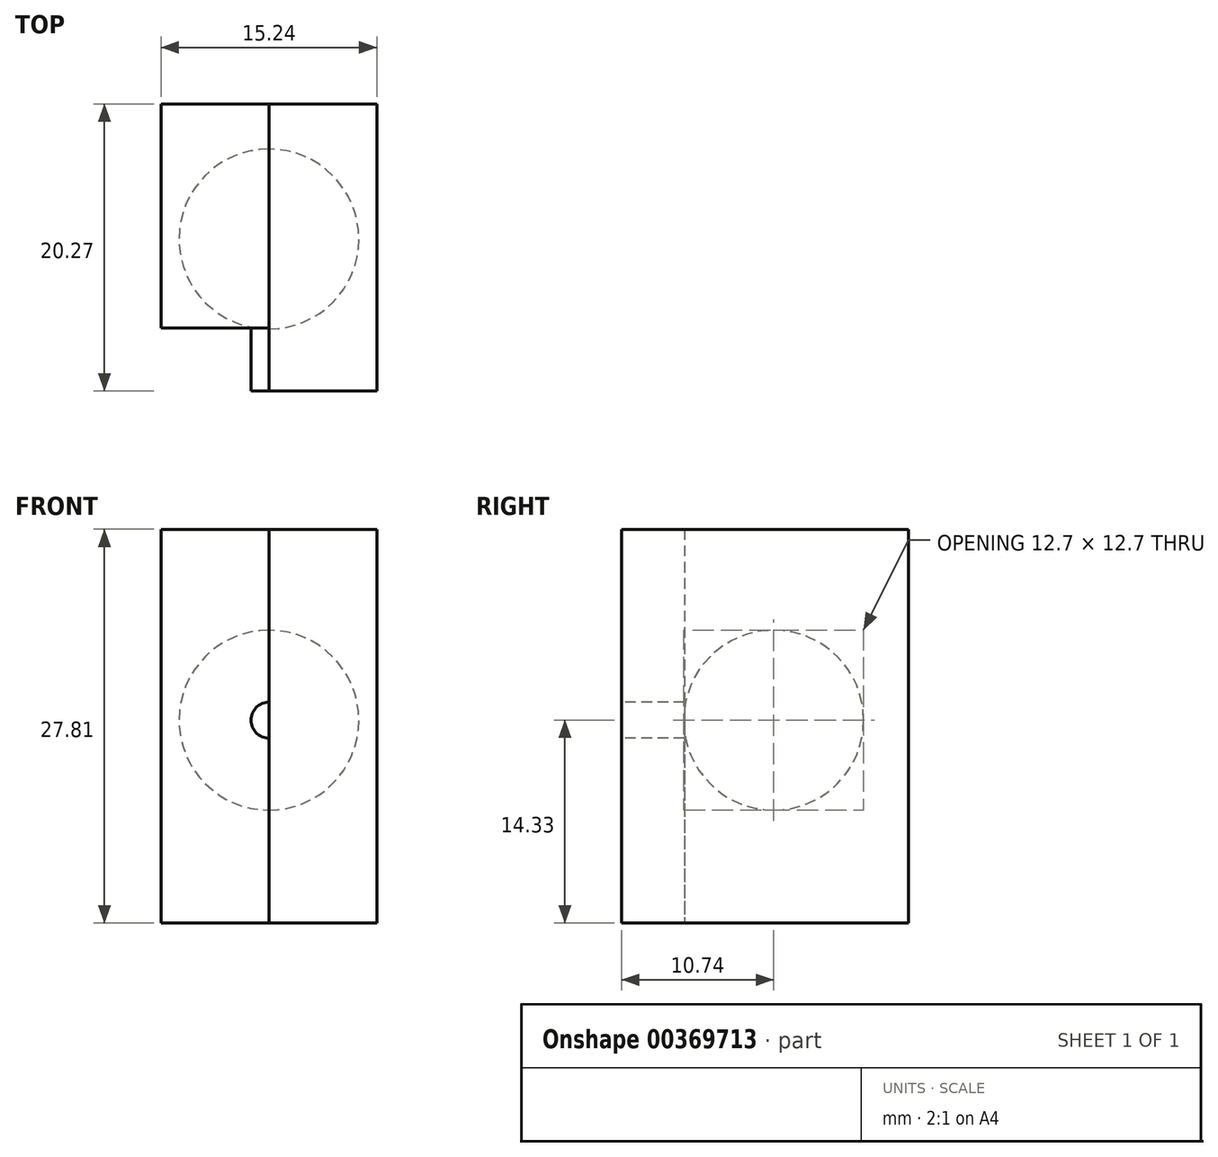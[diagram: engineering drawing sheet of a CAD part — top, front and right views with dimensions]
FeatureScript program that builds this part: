
annotation { "Feature Type Name" : "Feature", "Feature Type Description" : "" }
export const myFeature = defineFeature(function(context is Context, id is Id, definition is map)
    precondition{}
    {
        {
            var Q0;
            Q0=qCreatedBy(makeId("Top.planeOp"),FACE);
            var sketch = newSketch(context, id + "F0", { "sketchPlane" : qUnion([Q0])});
            skLineSegment(sketch, "E0", {"start": v(0, 0) * mm, "end": v(0, 12.7) * mm});
            skArc(sketch, "E1", {"start": v(0, 0) * mm, "mid": v(6.35, 6.35) * mm, "end": v(0, 12.7) * mm});
            skSolve(sketch);
        }
        {
            var Q0;
            Q0=makeQuery(id+"F0.imprint","IMPRINT",FACE,{"disambiguationData":[TD([[makeQuery(id+"F0.imprint","IMPRINT",EDGE,{"derivedFrom":sQuery(id+"F0.wireOp",EDGE,"E0")}),-1.0]])]});
            var Q1;
            Q1=sQuery(id+"F0.wireOp",EDGE,"E0");
            revolve(context, id + "F1", {"entities" : qUnion([Q0]), "axis" : qUnion([Q1]), "revolveType" : RevolveType.FULL});
        }
        {
            var Q0;
            Q0=qCreatedBy(makeId("Right.planeOp"),FACE);
            var sketch = newSketch(context, id + "F2", { "sketchPlane" : qUnion([Q0])});
            skLineSegment(sketch, "E2.bottom", {"start": v(-4.39, 13.48) * mm, "end": v(15.88, 13.48) * mm});
            skLineSegment(sketch, "E2.top", {"start": v(-4.39, -14.33) * mm, "end": v(15.88, -14.33) * mm});
            skLineSegment(sketch, "E2.left", {"start": v(-4.39, 13.48) * mm, "end": v(-4.39, -14.33) * mm});
            skLineSegment(sketch, "E2.right", {"start": v(15.88, 13.48) * mm, "end": v(15.88, -14.33) * mm});
            skSolve(sketch);
        }
        {
            var Q0;
            Q0 = qSketchRegion(id + "F2", true);
            extrude(context, id + "F3", {"entities" : qUnion([Q0]), "depth" : 7.62 * mm});
        }
        {
            var Q0;
            Q0 = qSketchRegion(id + "F2", true);
            extrude(context, id + "F4", {"entities" : qUnion([Q0]), "oppositeDirection" : true, "depth" : 7.62 * mm});
        }
        {
            var Q0;
            Q0=makeQuery(id+"F1.opRevolve","SWEPT_BODY",BODY,{"disambiguationData":[OSD([sQuery(id+"F0.wireOp",EDGE,"E0"),sQuery(id+"F0.wireOp",EDGE,"E1")])]});
            var Q1;
            Q1=makeQuery(id+"F4.opExtrude","SWEPT_BODY",BODY,{"disambiguationData":[OSD([sQuery(id+"F2.wireOp",EDGE,"E2.bottom"),sQuery(id+"F2.wireOp",EDGE,"E2.top"),sQuery(id+"F2.wireOp",EDGE,"E2.left"),sQuery(id+"F2.wireOp",EDGE,"E2.right")])]});
            var Q2;
            Q2=makeQuery(id+"F3.opExtrude","SWEPT_BODY",BODY,{"disambiguationData":[OSD([sQuery(id+"F2.wireOp",EDGE,"E2.bottom"),sQuery(id+"F2.wireOp",EDGE,"E2.top"),sQuery(id+"F2.wireOp",EDGE,"E2.left"),sQuery(id+"F2.wireOp",EDGE,"E2.right")])]});
            booleanBodies(context, id + "F5", {"operationType" : BooleanOperationType.SUBTRACTION, "tools" : qUnion([Q0]), "targets" : qUnion([Q1, Q2])});
        }
        {
            var Q0;
            Q0=makeQuery(id+"F4.opExtrude","SWEPT_FACE",FACE,{"disambiguationData":[OSD([sQuery(id+"F2.wireOp",EDGE,"E2.left")])]});
            var sketch = newSketch(context, id + "F6", { "sketchPlane" : qUnion([Q0])});
            skArc(sketch, "E3", {"start": v(0, -1.27) * mm, "mid": v(-1.27, 0) * mm, "end": v(0, 1.27) * mm});
            skSolve(sketch);
        }
        {
            var Q0;
            {var subQ0=sQuery(id+"F6.wireOp",EDGE,"E3");Q0=makeQuery(id+"F6.imprint","IMPRINT",FACE,{"disambiguationData":[TD([[makeQuery(id+"F6.imprint","IMPRINT",EDGE,{"derivedFrom":subQ0}),-1.0]])]});}
            extrude(context, id + "F7", {"entities" : qUnion([Q0]), "operationType" : NewBodyOperationType.REMOVE, "oppositeDirection" : true, "depth" : 4.44 * mm});
        }
    });
